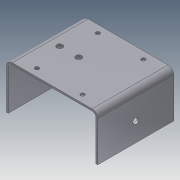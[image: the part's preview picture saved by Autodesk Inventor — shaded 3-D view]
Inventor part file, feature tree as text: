
AUTODESK INVENTOR PART (.ipt)
format: ipt  version: 2012 (Build 160160000, 160)  size: 116,224 bytes
history: native  units: in
note: dims shown in document units (in); Inventor stores cm internally (conversion verified against a paired STEP export)
features: hole x3, pattern_linear x2, extrude x1, sketch x1
ambient origin geometry x8: Origin, YZ Plane, XZ Plane, XY Plane, X Axis, Y Axis, Z Axis, Center Point
bodies: Solid1 (feature_tree)
feature tree (7):
  extrude  "Extrusion1"  Depth=0.1196in
  hole  "Hole1"  [1 undecoded]
  pattern_linear  "Rectangular Pattern1"  Spacing1=6.0in  [1 undecoded]
  hole  "Hole2"  [1 undecoded]
  hole  "Hole3"  [1 undecoded]
  pattern_linear  "Rectangular Pattern2"  Spacing1=5.0in  [1 undecoded]
  sketch  "Sketch1"  dims[d0=3.0in d1=0.1196in d2=0.1196in d3=6.0in d4=0.25in d5=0.375in d6=5.0in d7=0.0in d13=2.5in d14=1.0in d15=0.39in d16=0.75in d17=0.375in d18=0.25in d19=0.5635in d20=1.0in d21=0.8108in d22=0.7874in d24=1.25in d25=0.3937in d27=0.0in d28=1.25in d29=2.5in d30=0.39in d31=0.75in d32=0.375in d33=0.25in d34=0.5635in d35=1.0in d36=0.8108in d37=1.5in d38=0.5in d39=0.265in d40=0.75in d41=0.375in d42=0.25in d43=0.5635in d44=1.0in d45=0.8108in d46=0.7874in d48=3.0in d49=0.7874in d51=4.0in]
note: 5 required parameter values undecoded (feature->parameter linkage not recoverable at this tier; creation-order binding heuristic only, values carry confidence <= 0.55)
